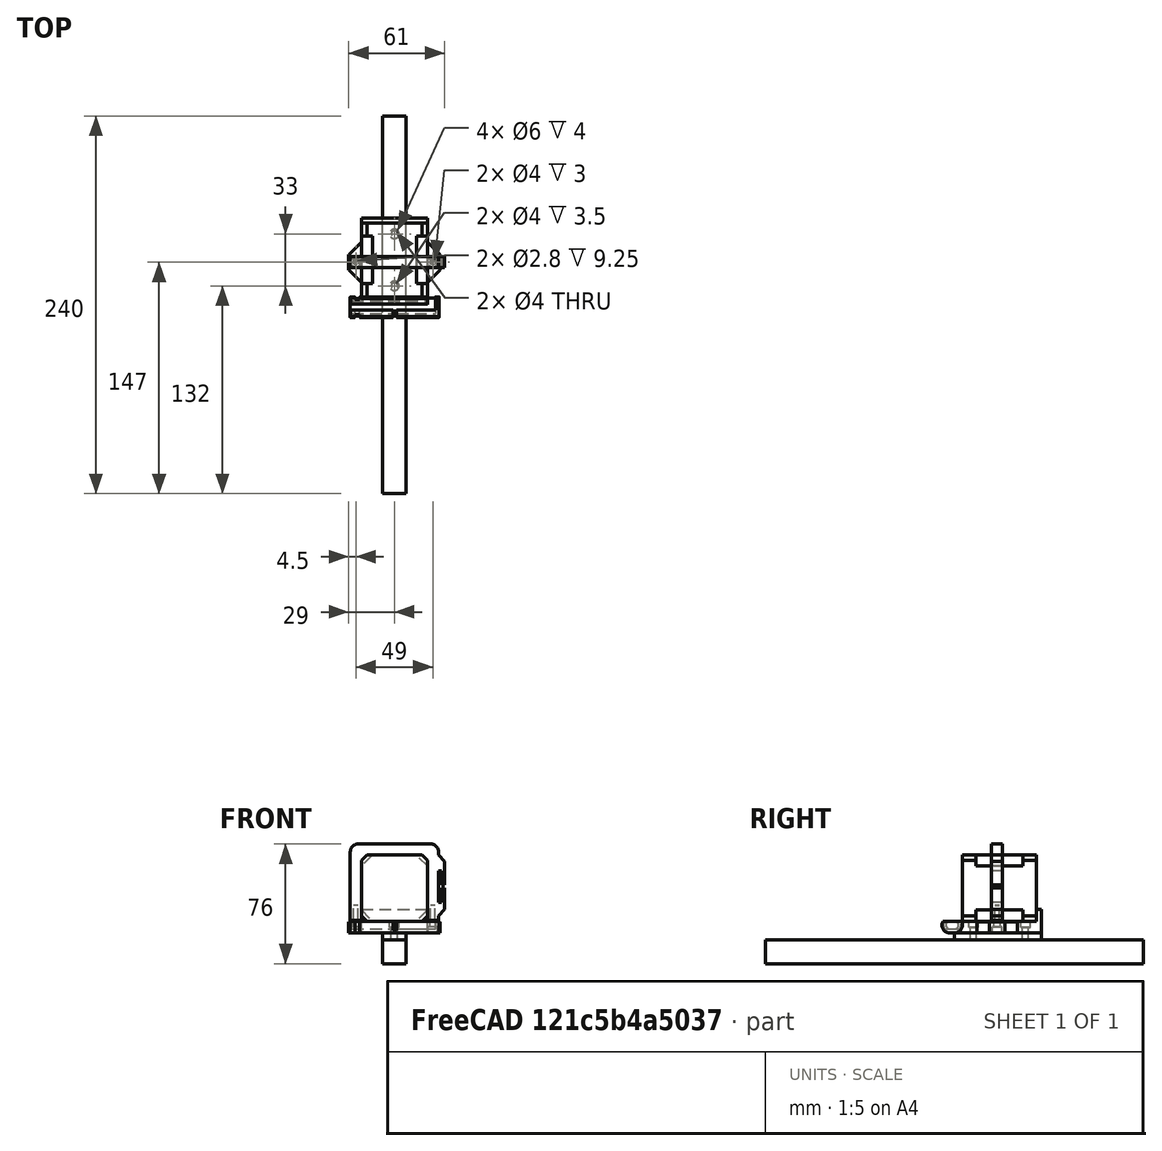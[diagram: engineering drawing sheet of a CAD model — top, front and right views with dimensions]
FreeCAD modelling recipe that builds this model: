
FCSTD DOCUMENT  (FreeCAD 0.14R3703 (Git))
Label: GOUM_Extruder_Holder2
License: CC-BY 3.0
LicenseURL: http://creativecommons.org/licenses/by/3.0/
objects: Part::Cylinder×21, Part::Cut×18, Part::Box×16, Part::MultiFuse×9, Part::Chamfer×4, Part::Fillet×3
note: 71 computed .brp shape members not serialized (recipe doc carries the construction recipe); baked Part::Feature solids carry a one-line shape summary decoded from their .brp

FEATURE [Part::Cylinder] Cylinder002  label="cable-tunnel-outer-shell"
  Angle = 360
  Height = 56.5
  Placement = pos=(0,0,0) rot=(0,1,0;1.5708rad)
  Radius = 5
FEATURE [Part::Box] Box001  label="DO_NOT_PRINT_Z-Tower"
  Height = 15
  Length = 15
  Placement = pos=(20.5,-120,-24.5) rot=(0,0,1;0rad)
  Width = 240
FEATURE [Part::Box] Box002  label="Z-Distance-uncut"
  Height = 4.5
  Length = 15
  Placement = pos=(20.5,0,-9) rot=(0,0,1;0rad)
  Width = 55
FEATURE [Part::Box] Box005  label="cut-endstop-cable"
  Height = 10
  Length = 2.5
  Placement = pos=(27,-8,-2.5) rot=(0,0,1;0rad)
  Width = 5
FEATURE [Part::Box] Box007  label="base-plate1"
  Height = 7.5
  Length = 42
  Placement = pos=(7,4,-5) rot=(0,0,1;0rad)
  Width = 48
FEATURE [Part::Box] Box008  label="nema17-support"
  Height = 15
  Length = 42
  Placement = pos=(7,52,-5) rot=(0,0,1;0rad)
  Width = 3
FEATURE [Part::Box] Box011  label="fill1"
  Height = 5
  Length = 42
  Placement = pos=(7,0,-5) rot=(0,0,1;0rad)
  Width = 5
FEATURE [Part::Cut] Cut  label="fill-cut1"
  Base = -> Box011
  Tool = -> Cylinder002
FEATURE [Part::Box] Box  label="nema17-body"
  Height = 42
  Length = 42
  Placement = pos=(7,13.5,2.5) rot=(0,0,1;0rad)
  Width = 30
FEATURE [Part::Box] Box012  label="nema17-top"
  Height = 42
  Length = 42
  Placement = pos=(7,5,2.5) rot=(0,0,1;0rad)
  Width = 8.5
FEATURE [Part::Box] Box013  label="nema17-bottom"
  Height = 42
  Length = 42
  Placement = pos=(7,43.5,2.5) rot=(0,0,1;0rad)
  Width = 8.5
FEATURE [Part::Chamfer] Chamfer
  Base = -> Box012
  Edges = 4 edges r=3.5: [Edge2,Edge4,Edge6,Edge8]
FEATURE [Part::Chamfer] Chamfer001
  Base = -> Box013
  Edges = 4 edges r=3.5: [Edge2,Edge4,Edge6,Edge8]
FEATURE [Part::Chamfer] Chamfer002
  Base = -> Box
  Edges = 4 edges r=7: [Edge2,Edge4,Edge6,Edge8]
FEATURE [Part::MultiFuse] Fusion  label="DO_NOT_PRINT_Nema17-Dummy"
  Shapes = -> [Chamfer,Chamfer001,Chamfer002]
FEATURE [Part::Box] Box014  label="hold1"
  Height = 7
  Length = 10
  Placement = pos=(-1,22,-5) rot=(0,0,1;0rad)
  Width = 10
FEATURE [Part::Box] Box015  label="hold2"
  Height = 7
  Length = 10
  Placement = pos=(47,22,-5) rot=(0,0,1;0rad)
  Width = 10
FEATURE [Part::Cylinder] Cylinder
  Angle = 360
  Height = 7
  Radius = 3
FEATURE [Part::Cylinder] Cylinder003  label="Cylinder001"
  Angle = 360
  Height = 10
  Radius = 2
FEATURE [Part::MultiFuse] Fusion001  label="bolt-hole1"
  Placement = pos=(3.5,27,-8) rot=(0,0,1;0rad)
  Shapes = -> [Cylinder,Cylinder003]
FEATURE [Part::Cylinder] Cylinder004  label="Cylinder006"
  Angle = 360
  Height = 10
  Radius = 2
FEATURE [Part::Cylinder] Cylinder005
  Angle = 360
  Height = 7
  Radius = 3
FEATURE [Part::MultiFuse] Fusion002  label="bolt-hole2"
  Placement = pos=(52.5,27,-8) rot=(0,0,1;0rad)
  Shapes = -> [Cylinder005,Cylinder004]
FEATURE [Part::Cylinder] Cylinder006  label="Cylinder007"
  Angle = 360
  Height = 11.5
  Radius = 2
FEATURE [Part::Cylinder] Cylinder007  label="Cylinder008"
  Angle = 360
  Height = 4
  Placement = pos=(0,0,7.5) rot=(0,0,1;0rad)
  Radius = 3
FEATURE [Part::MultiFuse] Fusion003  label="bolt-hole3"
  Placement = pos=(28,12,-9) rot=(0,0,1;0rad)
  Shapes = -> [Cylinder006,Cylinder007]
FEATURE [Part::Cylinder] Cylinder008  label="Cylinder011"
  Angle = 360
  Height = 4
  Placement = pos=(0,0,7.5) rot=(0,0,1;0rad)
  Radius = 3
FEATURE [Part::Cylinder] Cylinder009  label="Cylinder012"
  Angle = 360
  Height = 11.5
  Radius = 2
FEATURE [Part::MultiFuse] Fusion004  label="bolt-hole4"
  Placement = pos=(28,45,-9) rot=(0,0,1;0rad)
  Shapes = -> [Cylinder009,Cylinder008]
FEATURE [Part::Cylinder] Cylinder010  label="Cylinder014"
  Angle = 360
  Height = 4
  Placement = pos=(0,0,7.5) rot=(0,0,1;0rad)
  Radius = 4
FEATURE [Part::Cylinder] Cylinder011  label="Cylinder010"
  Angle = 360
  Height = 11.5
  Radius = 2
FEATURE [Part::MultiFuse] Fusion005  label="bolt-hole3-distance"
  Placement = pos=(28,12,-9) rot=(0,0,1;0rad)
  Shapes = -> [Cylinder011,Cylinder010]
FEATURE [Part::Cylinder] Cylinder012  label="Cylinder015"
  Angle = 360
  Height = 4
  Placement = pos=(0,0,7.5) rot=(0,0,1;0rad)
  Radius = 4
FEATURE [Part::Cylinder] Cylinder013  label="Cylinder016"
  Angle = 360
  Height = 11.5
  Radius = 2
FEATURE [Part::MultiFuse] Fusion006  label="bolt-hole4-distance"
  Placement = pos=(28,45,-9) rot=(0,0,1;0rad)
  Shapes = -> [Cylinder013,Cylinder012]
FEATURE [Part::Cut] Cut012
  Base = -> Box002
  Tool = -> Fusion005
FEATURE [Part::Cut] Cut013  label="Z-Distance"
  Base = -> Cut012
  Placement = pos=(0,0,-0.5) rot=(0,0,1;0rad)
  Tool = -> Fusion006
FEATURE [Part::Cylinder] Cylinder014  label="cable-tunnel-inner-lower"
  Angle = 180
  Height = 54
  Radius = 2.5
FEATURE [Part::Cylinder] Cylinder015  label="cable-tunnel-outer-lower"
  Angle = 180
  Height = 56.5
  Radius = 5
FEATURE [Part::Cylinder] Cylinder016  label="cable-tunnel-outer-upper"
  Angle = 180
  Height = 56.5
  Placement = pos=(0,0,0) rot=(0,0,1;3.14159rad)
  Radius = 5
FEATURE [Part::Cylinder] Cylinder017  label="cable-tunnel-inner-upper"
  Angle = 180
  Height = 54
  Placement = pos=(0,0,0) rot=(0,0,1;3.14159rad)
  Radius = 2.5
FEATURE [Part::Cylinder] Cylinder018  label="cable-tunnel-ziptie-outer-lower"
  Angle = 180
  Height = 3
  Placement = pos=(0,0,3) rot=(0,0,1;0rad)
  Radius = 5
FEATURE [Part::Cylinder] Cylinder019  label="cable-tunnel-ziptie-outer-upper"
  Angle = 180
  Height = 3
  Placement = pos=(0,0,3) rot=(0,0,1;3.14159rad)
  Radius = 5
FEATURE [Part::Cylinder] Cylinder020  label="cable-tunnel-ziptie-inner-lower"
  Angle = 180
  Height = 3
  Placement = pos=(0,-1,3) rot=(0,0,1;0rad)
  Radius = 5
FEATURE [Part::Cylinder] Cylinder021  label="cable-tunnel-ziptie-inner-upper"
  Angle = 180
  Height = 3
  Placement = pos=(0,1,3) rot=(0,0,1;3.14159rad)
  Radius = 5
FEATURE [Part::Cut] Cut014  label="cable-tunnel-ziptie-upper-groove"
  Base = -> Cylinder019
  Tool = -> Cylinder021
FEATURE [Part::Cut] Cut015  label="cable-tunnel-ziptie-lower-groove"
  Base = -> Cylinder018
  Tool = -> Cylinder020
FEATURE [Part::Cut] Cut016
  Base = -> Cylinder015
  Tool = -> Cylinder014
FEATURE [Part::Cut] Cut017  label="cable-tunnel-lower"
  Base = -> Cut016
  Tool = -> Cut015
FEATURE [Part::Cut] Cut018
  Base = -> Cylinder016
  Tool = -> Cylinder017
FEATURE [Part::Cut] Cut019  label="cable-tunnel-upper"
  Base = -> Cut018
  Placement = pos=(0,-3,0) rot=(0,0,1;0rad)
  Tool = -> Cut014
FEATURE [Part::Box] Box016  label="cable-tunnel-middle-outer"
  Height = 56.5
  Length = 10
  Placement = pos=(-5,-3,0) rot=(0,0,1;0rad)
  Width = 3
FEATURE [Part::Box] Box017  label="cable-tunnel-middle-inner"
  Height = 54
  Length = 5
  Placement = pos=(-2.5,-3,0) rot=(0,0,1;0rad)
  Width = 3
FEATURE [Part::Cut] Cut020  label="cable-tunnel-middle"
  Base = -> Box016
  Tool = -> Box017
FEATURE [Part::MultiFuse] Fusion007  label="cable-tunnel"
  Placement = pos=(0,0,0) rot=(0,1,0;1.5708rad)
  Shapes = -> [Cut017,Cut019,Cut020]
FEATURE [Part::Box] Box018  label="cut-cable-drop"
  Height = 10
  Length = 5
  Placement = pos=(49,0,-2.5) rot=(0,0,1;0rad)
  Width = 5
FEATURE [Part::Box] Box019  label="cut-open"
  Height = 10
  Length = 58
  Placement = pos=(-1,-8,2.45) rot=(0,0,1;0rad)
  Width = 13
FEATURE [Part::Cut] Cut021
  Base = -> Fusion007
  Tool = -> Box019
FEATURE [Part::Cut] Cut022
  Base = -> Cut021
  Tool = -> Box018
FEATURE [Part::Box] Box020  label="cut-endstop-cable45"
  Height = 10
  Length = 2.5
  Placement = pos=(27,-8,-4.5) rot=(1,0,0;0.785398rad)
  Width = 7.5
FEATURE [Part::Cut] Cut023
  Base = -> Cut022
  Tool = -> Box005
FEATURE [Part::Cut] Cut024
  Base = -> Cut023
  Tool = -> Box020
FEATURE [Part::Fillet] Fillet  label="cable-tunnel-cut"
  Base = -> Cut024
  Edges = 3 edges r=1: [Edge59,Edge89,Edge107]
FEATURE [Part::MultiFuse] Fusion008
  Shapes = -> [Fillet,Cut,Box007,Box008,Box015,Box014]
FEATURE [Part::Cut] Cut025
  Base = -> Fusion008
  Tool = -> Fusion001
FEATURE [Part::Cut] Cut026
  Base = -> Cut025
  Tool = -> Fusion002
FEATURE [Part::Cut] Cut027
  Base = -> Cut026
  Tool = -> Fusion003
FEATURE [Part::Cut] Cut028
  Base = -> Cut027
  Tool = -> Fusion004
FEATURE [Part::Chamfer] Chamfer003  label="Holder-with-cable-tunnel"
  Base = -> Cut028
  Edges = 4 edges r=7.95: [Edge6,Edge12,Edge94,Edge96]
FEATURE [Part::Fillet] Fillet002
  Base = -> Chamfer001
  Edges = 2 edges r=5: [Edge27,Edge92]
FEATURE [Part::Fillet] Fillet001  label="DO_NOT_PRINT_Holder-clamp"
  Base = -> Fillet002
  Edges = 2 edges r=0.25: [Edge39,Edge100]
  Placement = pos=(7,30.5,44.5) rot=(1,0,0;1.5708rad)
